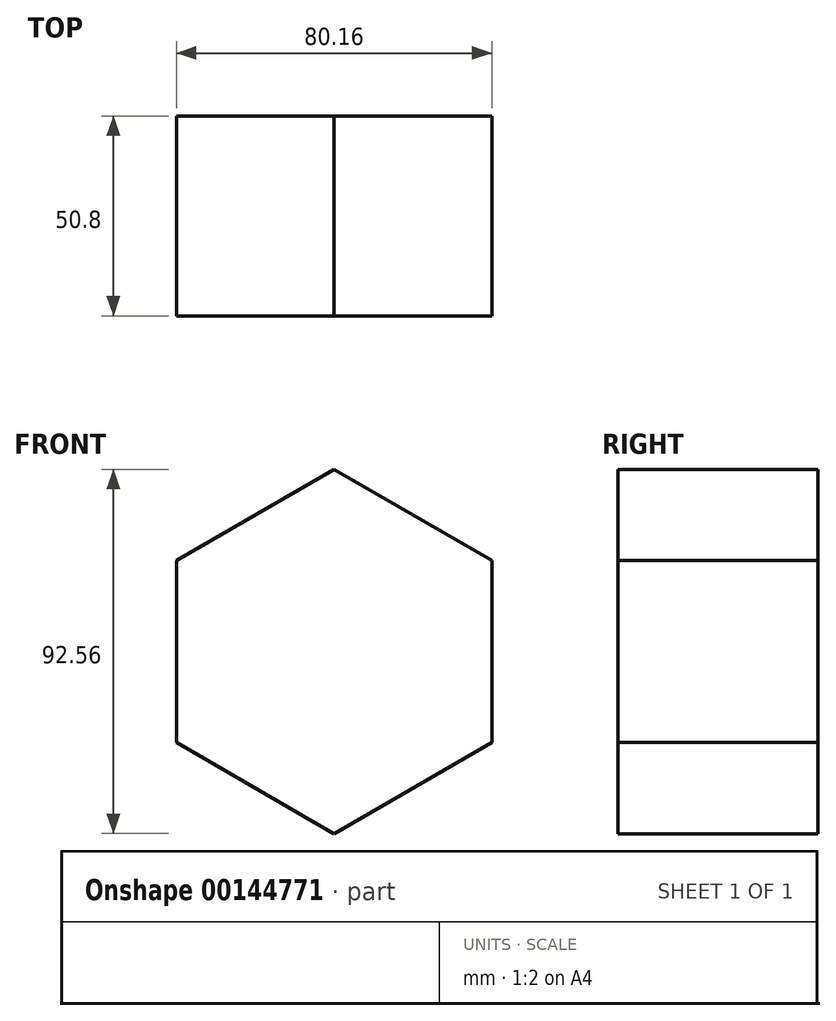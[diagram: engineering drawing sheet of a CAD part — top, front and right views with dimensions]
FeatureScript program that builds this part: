
annotation { "Feature Type Name" : "Feature", "Feature Type Description" : "" }
export const myFeature = defineFeature(function(context is Context, id is Id, definition is map)
    precondition{}
    {
        {
            var Q0;
            Q0=qCreatedBy(makeId("Front.planeOp"),FACE);
            var sketch = newSketch(context, id + "F1", { "sketchPlane" : qUnion([Q0])});
            skCircle(sketch, "E0.cCircle", {"center": v(0, 0) * mm, "radius": 40.08 * mm, "construction": true});
            skLineSegment(sketch, "E0.0", {"start": v(40.08, 23.14) * mm, "end": v(40.08, -23.14) * mm});
            skLineSegment(sketch, "E0.1", {"start": v(40.08, -23.14) * mm, "end": v(0, -46.28) * mm});
            skLineSegment(sketch, "E0.2", {"start": v(0, -46.28) * mm, "end": v(-40.08, -23.14) * mm});
            skLineSegment(sketch, "E0.3", {"start": v(-40.08, -23.14) * mm, "end": v(-40.08, 23.14) * mm});
            skLineSegment(sketch, "E0.4", {"start": v(-40.08, 23.14) * mm, "end": v(0, 46.28) * mm});
            skLineSegment(sketch, "E0.5", {"start": v(0, 46.28) * mm, "end": v(40.08, 23.14) * mm});
            skPoint(sketch, "E0.0.midPoint", {"position": v(40.08, 0) * mm});
            skSolve(sketch);
        }
        {
            var Q0;
            Q0=makeQuery(id+"F1.imprint","IMPRINT",FACE,{"disambiguationData":[TD([[makeQuery(id+"F1.imprint","IMPRINT",EDGE,{"derivedFrom":sQuery(id+"F1.wireOp",EDGE,"E0.0")}),-1.0]])]});
            extrude(context, id + "F0", {"entities" : qUnion([Q0]), "depth" : 50.8 * mm});
        }
    });
